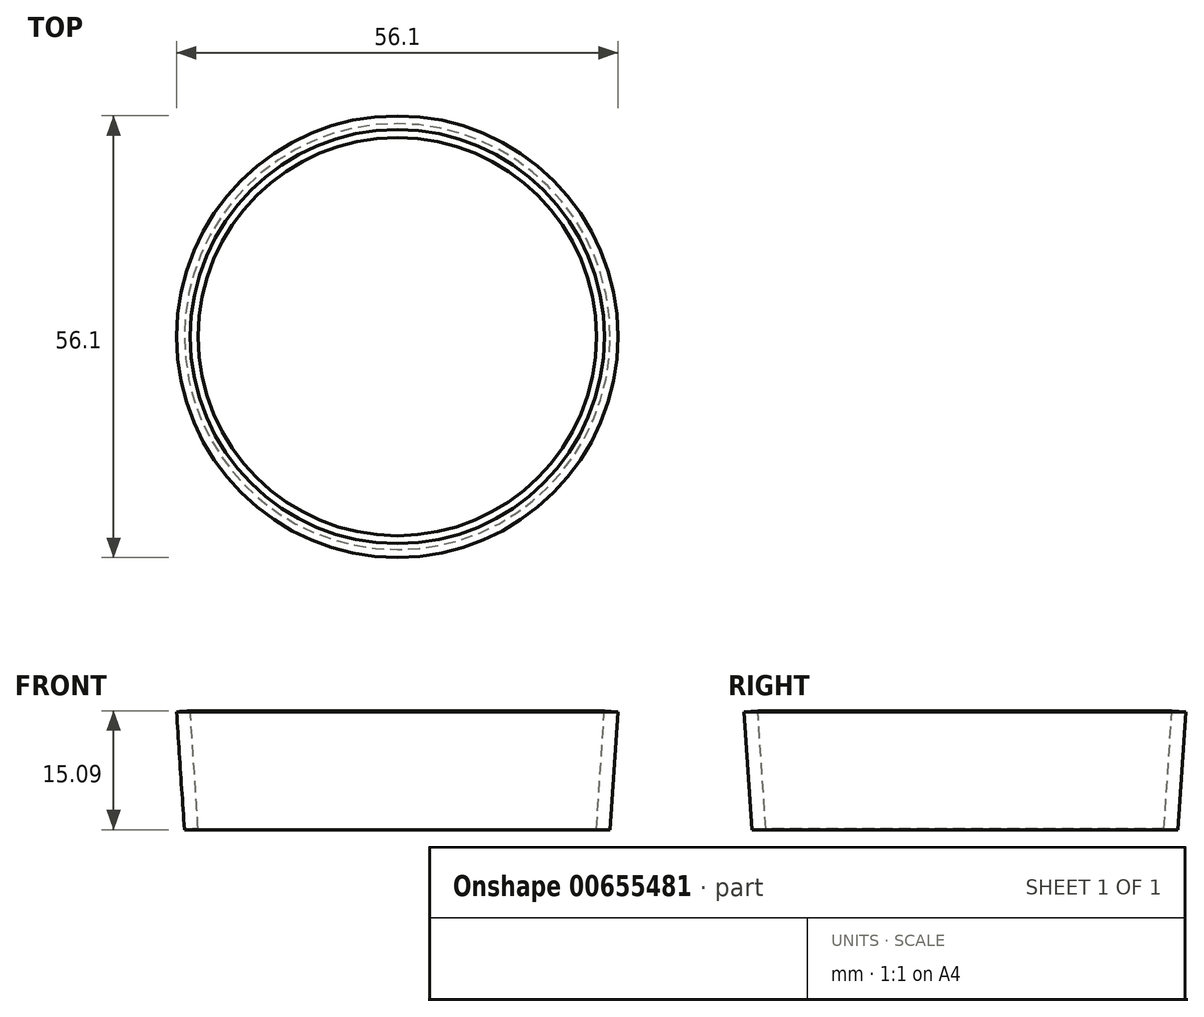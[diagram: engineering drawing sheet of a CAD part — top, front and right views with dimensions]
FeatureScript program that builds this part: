
annotation { "Feature Type Name" : "Feature", "Feature Type Description" : "" }
export const myFeature = defineFeature(function(context is Context, id is Id, definition is map)
    precondition{}
    {
        {
            var Q0;
            Q0=qCreatedBy(makeId("Front.planeOp"),FACE);
            var sketch = newSketch(context, id + "F0", { "sketchPlane" : qUnion([Q0])});
            skLineSegment(sketch, "E0", {"start": v(25.3, 0) * mm, "end": v(26.3, 14.97) * mm});
            skLineSegment(sketch, "E1", {"start": v(0, 0) * mm, "end": v(25.3, 0) * mm, "construction": true});
            skLineSegment(sketch, "E2", {"start": v(25.3, 0) * mm, "end": v(27.05, -0.12) * mm});
            skLineSegment(sketch, "E3", {"start": v(27.05, -0.12) * mm, "end": v(28.05, 14.85) * mm});
            skLineSegment(sketch, "E4", {"start": v(28.05, 14.85) * mm, "end": v(26.3, 14.97) * mm});
            skSolve(sketch);
        }
        {
            var Q0;
            Q0=qCreatedBy(makeId("Front.planeOp"),FACE);
            var sketch = newSketch(context, id + "F1", { "sketchPlane" : qUnion([Q0])});
            skLineSegment(sketch, "E5", {"start": v(0, 0) * mm, "end": v(0, 35.07) * mm, "construction": true});
            skSolve(sketch);
        }
        {
            var Q0;
            Q0=makeQuery(id+"F0.imprint","IMPRINT",FACE,{"disambiguationData":[TD([[makeQuery(id+"F0.imprint","IMPRINT",EDGE,{"derivedFrom":sQuery(id+"F0.wireOp",EDGE,"E0")}),-1.0]])]});
            var Q1;
            Q1=sQuery(id+"F1.wireOp",EDGE,"E5");
            revolve(context, id + "F2", {"surfaceOperationType" : NewSurfaceOperationType.NEW, "entities" : qUnion([Q0]), "axis" : qUnion([Q1]), "revolveType" : RevolveType.FULL});
        }
    });
